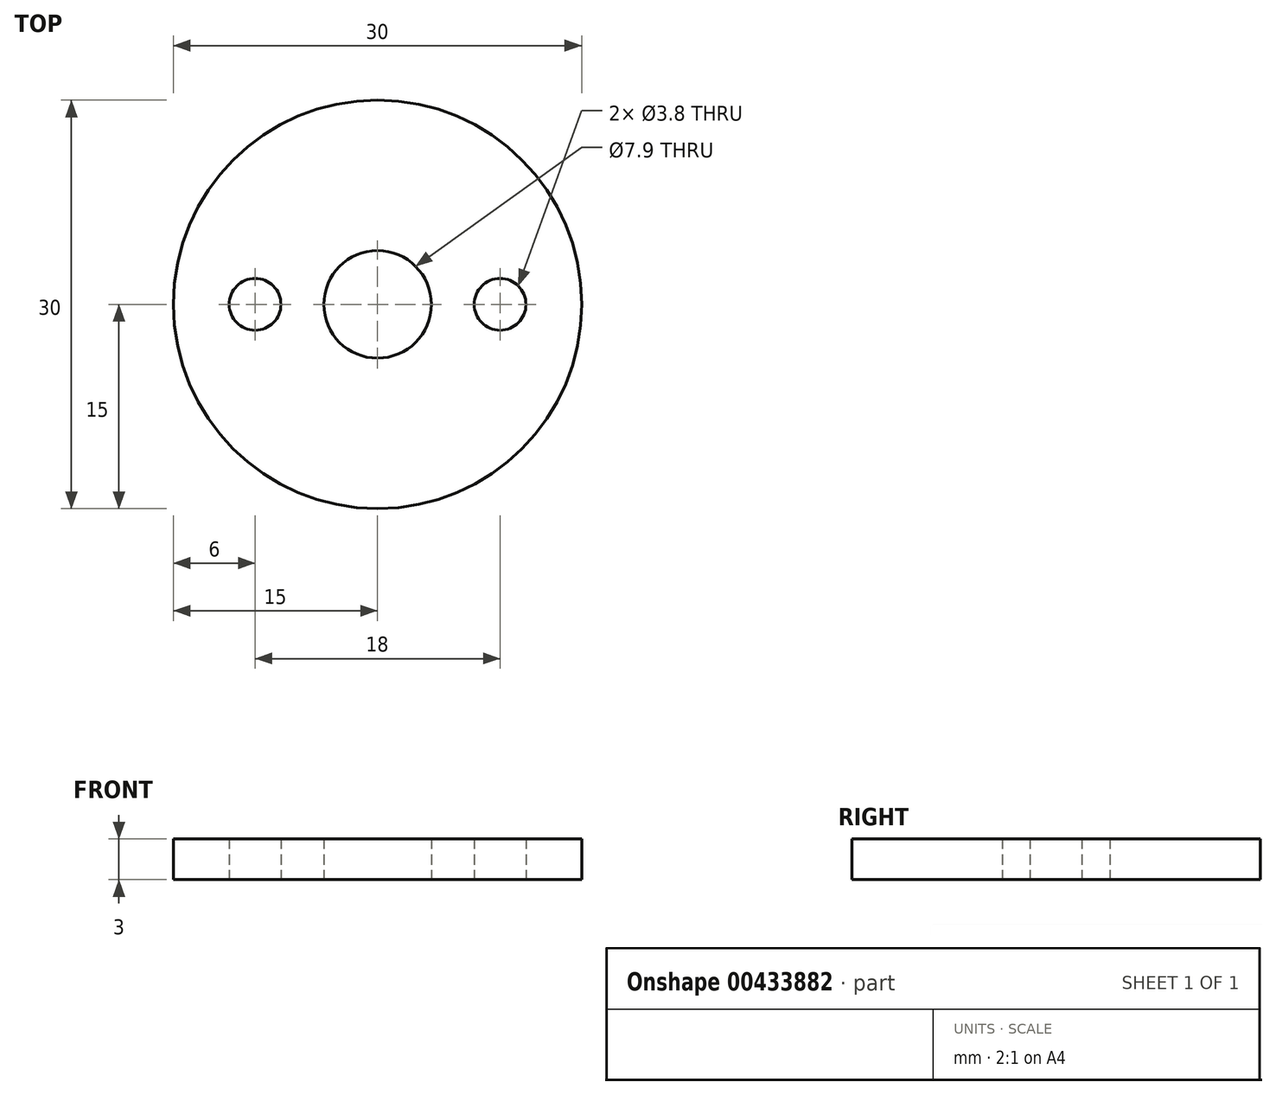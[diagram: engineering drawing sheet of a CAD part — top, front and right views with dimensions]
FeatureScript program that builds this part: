
annotation { "Feature Type Name" : "Feature", "Feature Type Description" : "" }
export const myFeature = defineFeature(function(context is Context, id is Id, definition is map)
    precondition{}
    {
        {
            var Q0;
            Q0=qCreatedBy(makeId("Top.planeOp"),FACE);
            var sketch = newSketch(context, id + "F0", { "sketchPlane" : qUnion([Q0])});
            skCircle(sketch, "E0", {"center": v(0, 0) * mm, "radius": 15 * mm});
            skCircle(sketch, "E1", {"center": v(-9, 0) * mm, "radius": 1.9 * mm});
            skCircle(sketch, "E2", {"center": v(9, 0) * mm, "radius": 1.9 * mm});
            skCircle(sketch, "E3", {"center": v(0, 0) * mm, "radius": 3.95 * mm});
            skSolve(sketch);
        }
        {
            var Q0;
            Q0 = qSketchRegion(id + "F0", true);
            extrude(context, id + "F1", {"entities" : qUnion([Q0]), "depth" : 3 * mm});
        }
    });
